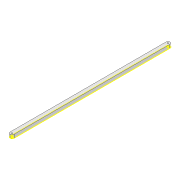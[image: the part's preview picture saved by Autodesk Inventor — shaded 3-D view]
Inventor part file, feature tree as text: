
AUTODESK INVENTOR PART (.ipt)
format: ipt  version: 2022 (Build 260153000, 153)  size: 94,720 bytes
history: native  units: mm
features: sketch x2, extrude x1, projected_geometry x1
ambient origin geometry x8: Origin, YZ Plane, XZ Plane, XY Plane, X Axis, Y Axis, Z Axis, Center Point
bodies: Solid1 (feature_tree)
feature tree (4):
  extrude  "Extrusion1"  Depth=10.0mm
  sketch  "Sketch2"  dims[d2=3.0mm d3=3.0mm d4=8.0mm d5=0.0mm]
  sketch  "Sketch1"  dims[d0=388.032mm d1=10.0mm]
  projected_geometry  "Projected Loop1"
